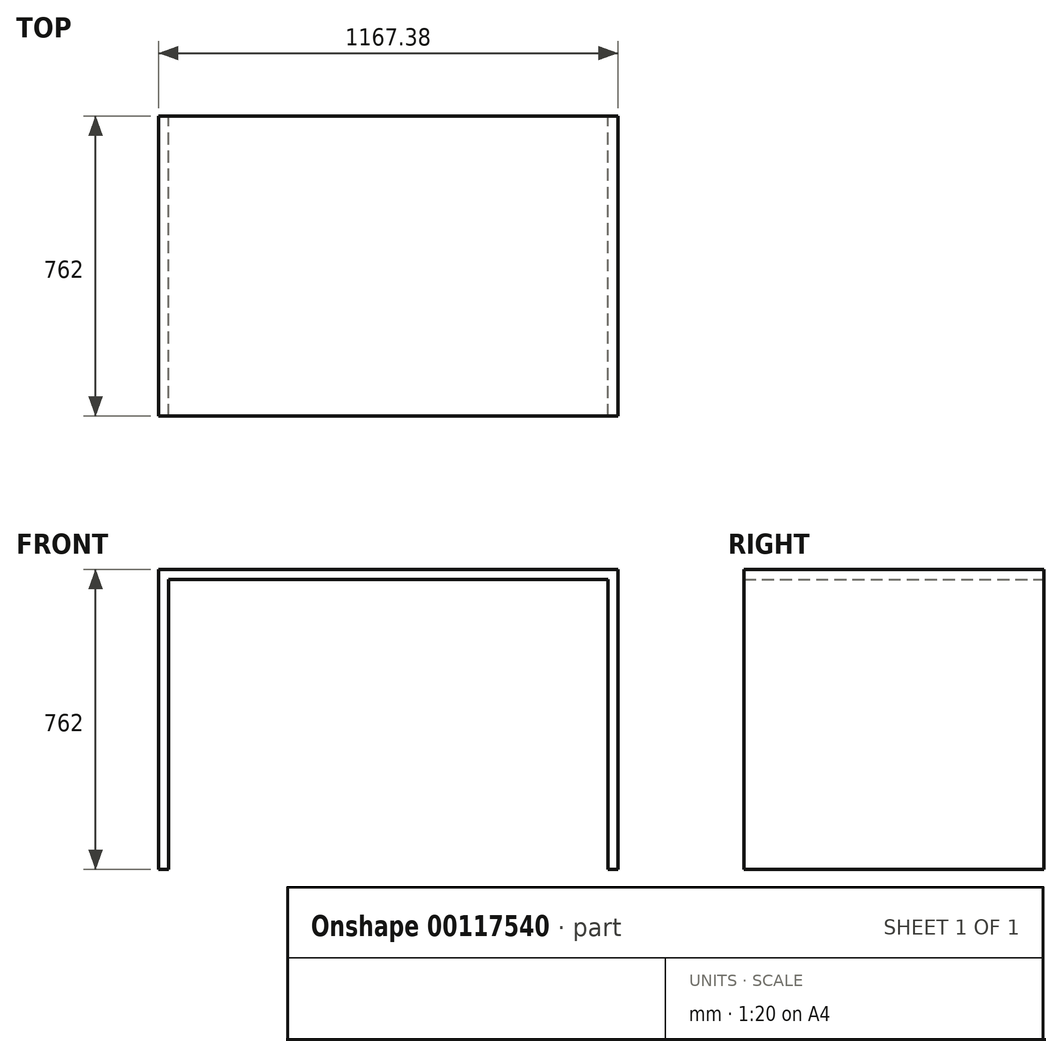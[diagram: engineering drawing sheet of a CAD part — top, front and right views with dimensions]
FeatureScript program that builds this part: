
annotation { "Feature Type Name" : "Feature", "Feature Type Description" : "" }
export const myFeature = defineFeature(function(context is Context, id is Id, definition is map)
    precondition{}
    {
        {
            var Q0;
            Q0=qCreatedBy(makeId("Front.planeOp"),FACE);
            var sketch = newSketch(context, id + "F0", { "sketchPlane" : qUnion([Q0])});
            skLineSegment(sketch, "E0.bottom", {"start": v(-583.7, -368.3) * mm, "end": v(-558.3, -368.3) * mm});
            skLineSegment(sketch, "E0.left", {"start": v(-583.7, -368.3) * mm, "end": v(-583.7, 393.7) * mm});
            skLineSegment(sketch, "E0.right", {"start": v(-558.3, -368.3) * mm, "end": v(-558.3, 368.3) * mm});
            skLineSegment(sketch, "E1.bottom", {"start": v(-583.7, 393.7) * mm, "end": v(583.7, 393.7) * mm});
            skLineSegment(sketch, "E1.top", {"start": v(-558.3, 368.3) * mm, "end": v(558.3, 368.3) * mm});
            skLineSegment(sketch, "E2.top", {"start": v(558.3, -368.3) * mm, "end": v(583.7, -368.3) * mm});
            skLineSegment(sketch, "E2.left", {"start": v(558.3, 368.3) * mm, "end": v(558.3, -368.3) * mm});
            skLineSegment(sketch, "E2.right", {"start": v(583.7, 393.7) * mm, "end": v(583.7, -368.3) * mm});
            skLineSegment(sketch, "E3", {"start": v(0, 368.3) * mm, "end": v(0, 393.7) * mm, "construction": true});
            skLineSegment(sketch, "E4", {"start": v(-1043.03, 0) * mm, "end": v(1043.03, 0) * mm, "construction": true});
            skPoint(sketch, "E5", {"position": v(-558.3, 0) * mm});
            skPoint(sketch, "E6", {"position": v(558.3, 0) * mm});
            skLineSegment(sketch, "E7", {"start": v(0, 0) * mm, "end": v(0, 736.6) * mm, "construction": true});
            skSolve(sketch);
        }
        {
            var Q0;
            Q0=makeQuery(id+"F0.imprint","IMPRINT",FACE,{"disambiguationData":[TD([[makeQuery(id+"F0.imprint","IMPRINT",EDGE,{"derivedFrom":sQuery(id+"F0.wireOp",EDGE,"E0.bottom")}),1.0]])]});
            extrude(context, id + "F1", {"entities" : qUnion([Q0]), "endBound" : BoundingType.SYMMETRIC, "depth" : 762 * mm});
        }
    });
